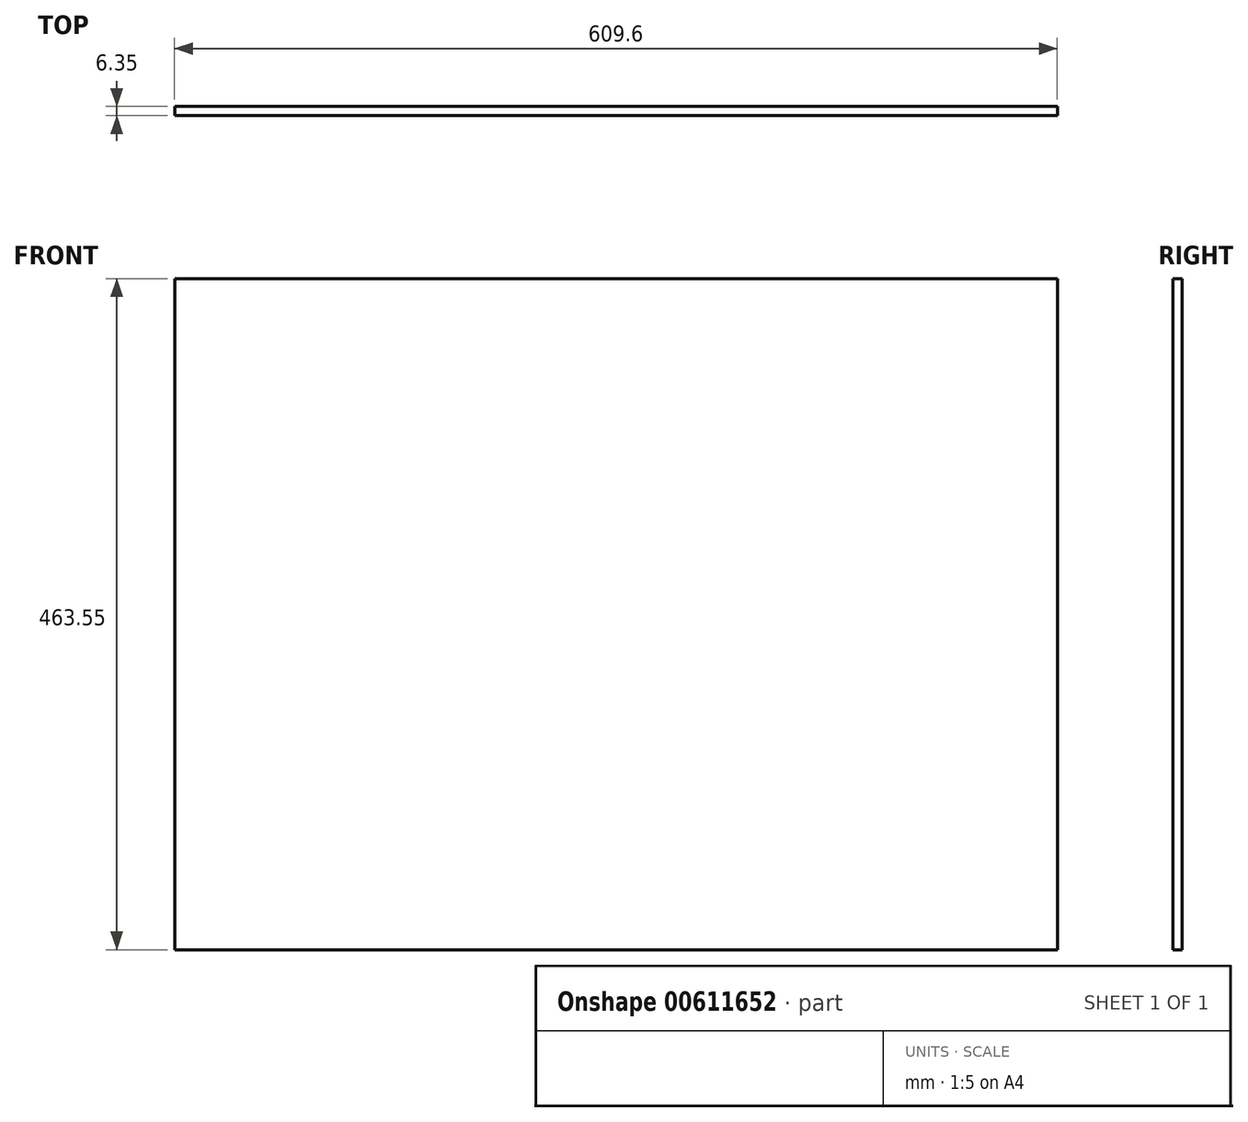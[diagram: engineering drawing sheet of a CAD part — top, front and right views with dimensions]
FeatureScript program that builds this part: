
annotation { "Feature Type Name" : "Feature", "Feature Type Description" : "" }
export const myFeature = defineFeature(function(context is Context, id is Id, definition is map)
    precondition{}
    {
        {
            var Q0;
            Q0=qCreatedBy(makeId("Front.planeOp"),FACE);
            var sketch = newSketch(context, id + "F0", { "sketchPlane" : qUnion([Q0])});
            skLineSegment(sketch, "E0", {"start": v(-13.14, 455.02) * mm, "end": v(-13.14, -8.53) * mm});
            skLineSegment(sketch, "E1", {"start": v(-13.14, -8.53) * mm, "end": v(596.46, -8.53) * mm});
            skLineSegment(sketch, "E2", {"start": v(596.46, -8.53) * mm, "end": v(596.46, 455.02) * mm});
            skLineSegment(sketch, "E3", {"start": v(596.46, 455.02) * mm, "end": v(-13.14, 455.02) * mm});
            skSolve(sketch);
        }
        {
            var Q0;
            Q0 = qSketchRegion(id + "F0", true);
            var Q1;
            Q1=makeQuery(id+"F0.imprint","IMPRINT",FACE,{"disambiguationData":[TD([[makeQuery(id+"F0.imprint","IMPRINT",EDGE,{"derivedFrom":sQuery(id+"F0.wireOp",EDGE,"E0")}),1.0]])]});
            extrude(context, id + "F1", {"entities" : qUnion([Q0, Q1]), "depth" : 6.35 * mm, "offsetDistance" : 25 * mm});
        }
    });
